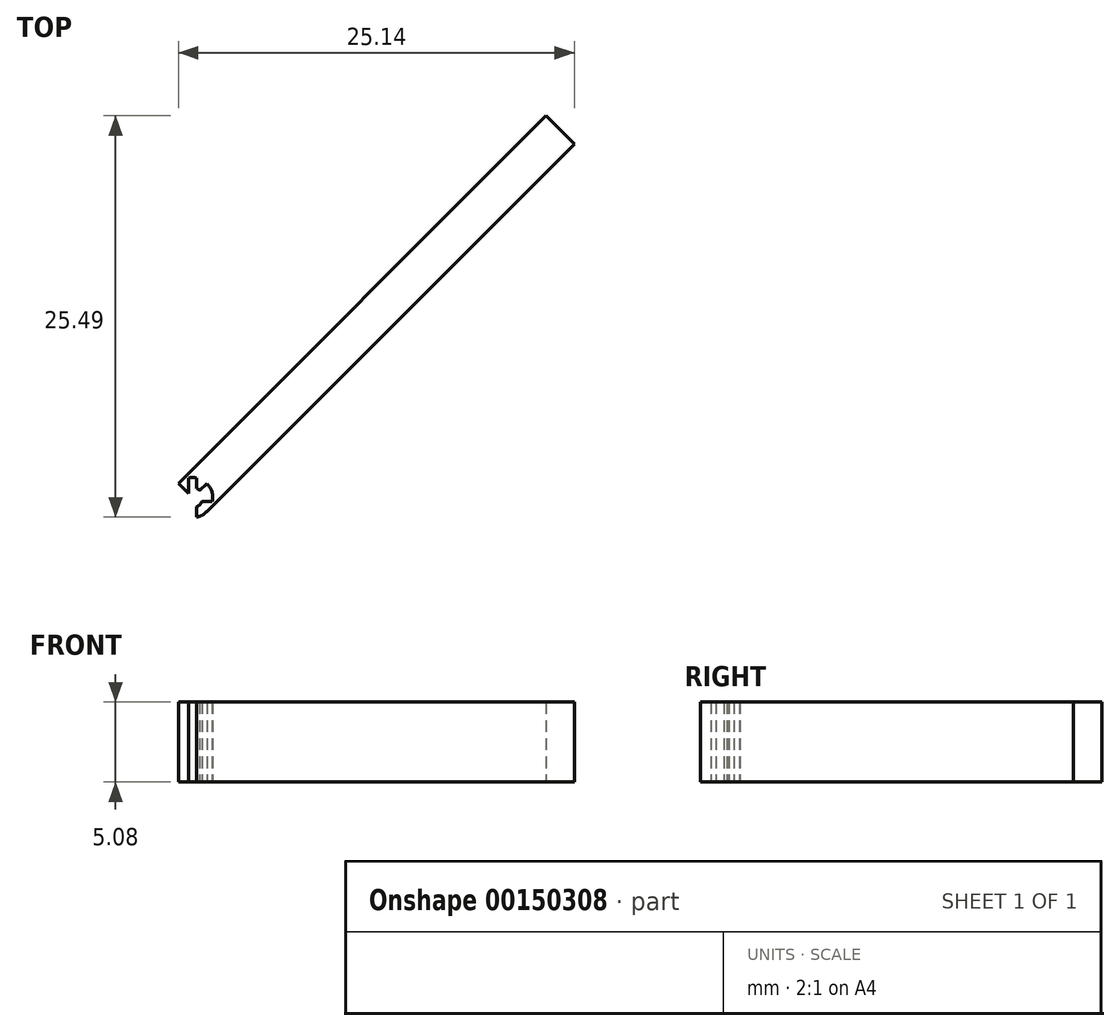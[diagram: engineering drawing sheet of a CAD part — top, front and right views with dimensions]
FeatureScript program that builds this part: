
annotation { "Feature Type Name" : "Feature", "Feature Type Description" : "" }
export const myFeature = defineFeature(function(context is Context, id is Id, definition is map)
    precondition{}
    {
        {
            var Q0;
            Q0=qCreatedBy(makeId("Top.planeOp"),FACE);
            var sketch = newSketch(context, id + "F0", { "sketchPlane" : qUnion([Q0])});
            skCircle(sketch, "E0", {"center": v(0, 0) * mm, "radius": 0.64 * mm});
            skCircle(sketch, "E1", {"center": v(0, 0) * mm, "radius": 1.27 * mm});
            skLineSegment(sketch, "E2.bottom", {"start": v(2.23, -1.87) * mm, "end": v(-1.87, 2.23) * mm});
            skLineSegment(sketch, "E2.top", {"start": v(1.87, -2.23) * mm, "end": v(-2.23, 1.87) * mm});
            skLineSegment(sketch, "E2.left", {"start": v(2.23, -1.87) * mm, "end": v(1.87, -2.23) * mm});
            skLineSegment(sketch, "E2.right", {"start": v(-1.87, 2.23) * mm, "end": v(-2.23, 1.87) * mm});
            skLineSegment(sketch, "E3.bottom", {"start": v(1.27, 0) * mm, "end": v(-1.27, 0) * mm});
            skLineSegment(sketch, "E3.top", {"start": v(1.27, 33.02) * mm, "end": v(-1.27, 33.02) * mm});
            skLineSegment(sketch, "E3.left", {"start": v(1.27, 0) * mm, "end": v(1.27, 33.02) * mm});
            skLineSegment(sketch, "E3.right", {"start": v(-1.27, 0) * mm, "end": v(-1.27, 33.02) * mm});
            skLineSegment(sketch, "E4", {"start": v(0, 0) * mm, "end": v(0.18, 0.18) * mm});
            skLineSegment(sketch, "E5", {"start": v(0, 0) * mm, "end": v(0, 1.27) * mm});
            skLineSegment(sketch, "E6.MirrorCS", {"start": v(-2.23, -1.87) * mm, "end": v(1.87, 2.23) * mm});
            skLineSegment(sketch, "E7.MirrorCS", {"start": v(-1.87, -2.23) * mm, "end": v(2.23, 1.87) * mm});
            skSolve(sketch);
        }
        {
            var Q0;
            {var subQ0=sQuery(id+"F0.wireOp",EDGE,"BzvpPFvM-H8qJ-Yu4j-K87A-fSPP2zc7mDrv.left");var subQ1=sQuery(id+"F0.wireOp",EDGE,"E0");var subQ2=makeQuery(id+"F0.imprint","INTERSECT",VERTEX,{"disambiguationData":[OD(0.0)],"derivedFrom":[subQ1,subQ0]});Q0=makeQuery(id+"F0.imprint","IMPRINT",FACE,{"disambiguationData":[TD([[makeQuery(id+"F0.imprint","IMPRINT",EDGE,{"disambiguationData":[TD([[subQ2,-1.0]])],"derivedFrom":subQ1}),-1.0]])]});}
            var Q1;
            {var subQ0=sQuery(id+"F0.wireOp",EDGE,"BzvpPFvM-H8qJ-Yu4j-K87A-fSPP2zc7mDrv.right");var subQ1=sQuery(id+"F0.wireOp",EDGE,"E0");var subQ2=makeQuery(id+"F0.imprint","INTERSECT",VERTEX,{"disambiguationData":[OD(0.0)],"derivedFrom":[subQ1,subQ0]});Q1=makeQuery(id+"F0.imprint","IMPRINT",FACE,{"disambiguationData":[TD([[makeQuery(id+"F0.imprint","IMPRINT",EDGE,{"disambiguationData":[TD([[subQ2,-1.0]])],"derivedFrom":subQ1}),-1.0]])]});}
            var Q2;
            {var subQ0=sQuery(id+"F0.wireOp",EDGE,"BzvpPFvM-H8qJ-Yu4j-K87A-fSPP2zc7mDrv.left");var subQ1=sQuery(id+"F0.wireOp",EDGE,"E0");var subQ2=makeQuery(id+"F0.imprint","INTERSECT",VERTEX,{"disambiguationData":[OD(0.0)],"derivedFrom":[subQ1,subQ0]});Q2=makeQuery(id+"F0.imprint","IMPRINT",FACE,{"disambiguationData":[TD([[makeQuery(id+"F0.imprint","IMPRINT",EDGE,{"disambiguationData":[TD([[subQ2,1.0]])],"derivedFrom":subQ1}),-1.0]])]});}
            var Q3;
            {var subQ0=sQuery(id+"F0.wireOp",EDGE,"E2.bottom");var subQ1=sQuery(id+"F0.wireOp",EDGE,"E0");var subQ2=makeQuery(id+"F0.imprint","INTERSECT",VERTEX,{"disambiguationData":[OD(1.0)],"derivedFrom":[subQ1,subQ0]});Q3=makeQuery(id+"F0.imprint","IMPRINT",FACE,{"disambiguationData":[TD([[makeQuery(id+"F0.imprint","IMPRINT",EDGE,{"disambiguationData":[TD([[subQ2,-1.0]])],"derivedFrom":subQ1}),-1.0]])]});}
            var Q4;
            {var subQ0=sQuery(id+"F0.wireOp",EDGE,"E2.bottom");var subQ1=sQuery(id+"F0.wireOp",EDGE,"E0");var subQ2=makeQuery(id+"F0.imprint","INTERSECT",VERTEX,{"disambiguationData":[OD(0.0)],"derivedFrom":[subQ1,subQ0]});Q4=makeQuery(id+"F0.imprint","IMPRINT",FACE,{"disambiguationData":[TD([[makeQuery(id+"F0.imprint","IMPRINT",EDGE,{"disambiguationData":[TD([[subQ2,1.0]])],"derivedFrom":subQ1}),-1.0]])]});}
            var Q5;
            {var subQ0=sQuery(id+"F0.wireOp",EDGE,"BzvpPFvM-H8qJ-Yu4j-K87A-fSPP2zc7mDrv.left");var subQ1=sQuery(id+"F0.wireOp",EDGE,"E0");var subQ2=makeQuery(id+"F0.imprint","INTERSECT",VERTEX,{"disambiguationData":[OD(1.0)],"derivedFrom":[subQ1,subQ0]});Q5=makeQuery(id+"F0.imprint","IMPRINT",FACE,{"disambiguationData":[TD([[makeQuery(id+"F0.imprint","IMPRINT",EDGE,{"disambiguationData":[TD([[subQ2,-1.0]])],"derivedFrom":subQ1}),-1.0]])]});}
            var Q6;
            {var subQ0=sQuery(id+"F0.wireOp",EDGE,"E2.top");var subQ1=sQuery(id+"F0.wireOp",EDGE,"E0");var subQ2=makeQuery(id+"F0.imprint","INTERSECT",VERTEX,{"disambiguationData":[OD(0.0)],"derivedFrom":[subQ1,subQ0]});Q6=makeQuery(id+"F0.imprint","IMPRINT",FACE,{"disambiguationData":[TD([[makeQuery(id+"F0.imprint","IMPRINT",EDGE,{"disambiguationData":[TD([[subQ2,-1.0]])],"derivedFrom":subQ1}),-1.0]])]});}
            var Q7;
            {var subQ0=sQuery(id+"F0.wireOp",EDGE,"BzvpPFvM-H8qJ-Yu4j-K87A-fSPP2zc7mDrv.right");var subQ1=sQuery(id+"F0.wireOp",EDGE,"E0");var subQ2=makeQuery(id+"F0.imprint","INTERSECT",VERTEX,{"disambiguationData":[OD(1.0)],"derivedFrom":[subQ1,subQ0]});Q7=makeQuery(id+"F0.imprint","IMPRINT",FACE,{"disambiguationData":[TD([[makeQuery(id+"F0.imprint","IMPRINT",EDGE,{"disambiguationData":[TD([[subQ2,-1.0]])],"derivedFrom":subQ1}),-1.0]])]});}
            var Q8;
            {var subQ0=sQuery(id+"F0.wireOp",EDGE,"BzvpPFvM-H8qJ-Yu4j-K87A-fSPP2zc7mDrv.right");var subQ1=sQuery(id+"F0.wireOp",EDGE,"E0");var subQ2=makeQuery(id+"F0.imprint","INTERSECT",VERTEX,{"disambiguationData":[OD(0.0)],"derivedFrom":[subQ1,subQ0]});Q8=makeQuery(id+"F0.imprint","IMPRINT",FACE,{"disambiguationData":[TD([[makeQuery(id+"F0.imprint","IMPRINT",EDGE,{"disambiguationData":[TD([[subQ2,-1.0]])],"derivedFrom":subQ1}),1.0]])]});}
            var Q9;
            {var subQ0=sQuery(id+"F0.wireOp",EDGE,"BzvpPFvM-H8qJ-Yu4j-K87A-fSPP2zc7mDrv.left");var subQ1=sQuery(id+"F0.wireOp",EDGE,"E0");var subQ2=makeQuery(id+"F0.imprint","INTERSECT",VERTEX,{"disambiguationData":[OD(0.0)],"derivedFrom":[subQ1,subQ0]});Q9=makeQuery(id+"F0.imprint","IMPRINT",FACE,{"disambiguationData":[TD([[makeQuery(id+"F0.imprint","IMPRINT",EDGE,{"disambiguationData":[TD([[subQ2,1.0]])],"derivedFrom":subQ1}),1.0]])]});}
            var Q10;
            {var subQ0=sQuery(id+"F0.wireOp",EDGE,"E2.top");var subQ1=sQuery(id+"F0.wireOp",EDGE,"E0");var subQ2=makeQuery(id+"F0.imprint","INTERSECT",VERTEX,{"disambiguationData":[OD(0.0)],"derivedFrom":[subQ1,subQ0]});Q10=makeQuery(id+"F0.imprint","IMPRINT",FACE,{"disambiguationData":[TD([[makeQuery(id+"F0.imprint","IMPRINT",EDGE,{"disambiguationData":[TD([[subQ2,-1.0]])],"derivedFrom":subQ1}),1.0]])]});}
            var Q11;
            {var subQ0=sQuery(id+"F0.wireOp",EDGE,"BzvpPFvM-H8qJ-Yu4j-K87A-fSPP2zc7mDrv.left");var subQ1=sQuery(id+"F0.wireOp",EDGE,"E0");var subQ2=makeQuery(id+"F0.imprint","INTERSECT",VERTEX,{"disambiguationData":[OD(1.0)],"derivedFrom":[subQ1,subQ0]});Q11=makeQuery(id+"F0.imprint","IMPRINT",FACE,{"disambiguationData":[TD([[makeQuery(id+"F0.imprint","IMPRINT",EDGE,{"disambiguationData":[TD([[subQ2,-1.0]])],"derivedFrom":subQ1}),1.0]])]});}
            var Q12;
            {var subQ0=sQuery(id+"F0.wireOp",EDGE,"E3.bottom");var subQ1=sQuery(id+"F0.wireOp",EDGE,"E0");var subQ2=makeQuery(id+"F0.imprint","INTERSECT",VERTEX,{"disambiguationData":[OD(1.0)],"derivedFrom":[subQ1,subQ0]});Q12=makeQuery(id+"F0.imprint","IMPRINT",FACE,{"disambiguationData":[TD([[makeQuery(id+"F0.imprint","IMPRINT",EDGE,{"disambiguationData":[TD([[subQ2,-1.0]])],"derivedFrom":subQ1}),-1.0]])]});}
            var Q13;
            {var subQ0=sQuery(id+"F0.wireOp",EDGE,"E3.bottom");var subQ1=sQuery(id+"F0.wireOp",EDGE,"E0");var subQ2=makeQuery(id+"F0.imprint","INTERSECT",VERTEX,{"disambiguationData":[OD(0.0)],"derivedFrom":[subQ1,subQ0]});Q13=makeQuery(id+"F0.imprint","IMPRINT",FACE,{"disambiguationData":[TD([[makeQuery(id+"F0.imprint","IMPRINT",EDGE,{"disambiguationData":[TD([[subQ2,1.0]])],"derivedFrom":subQ1}),-1.0]])]});}
            var Q14;
            {var subQ5=sQuery(id+"F0.wireOp",EDGE,"BzvpPFvM-H8qJ-Yu4j-K87A-fSPP2zc7mDrv.bottom");Q14=makeQuery(id+"F0.imprint","IMPRINT",FACE,{"disambiguationData":[TD([[makeQuery(id+"F0.imprint","IMPRINT",EDGE,{"derivedFrom":subQ5}),1.0]])]});}
            var Q15;
            {var subQ10=sQuery(id+"F0.wireOp",EDGE,"BzvpPFvM-H8qJ-Yu4j-K87A-fSPP2zc7mDrv.bottom");Q15=makeQuery(id+"F0.imprint","IMPRINT",FACE,{"disambiguationData":[TD([[makeQuery(id+"F0.imprint","IMPRINT",EDGE,{"derivedFrom":subQ10}),-1.0]])]});}
            var Q16;
            {var subQ0=sQuery(id+"F0.wireOp",EDGE,"E3.right");var subQ3=sQuery(id+"F0.wireOp",EDGE,"E2.bottom");var subQ5=makeQuery(id+"F0.imprint","INTERSECT",VERTEX,{"derivedFrom":[subQ3,subQ0]});Q16=makeQuery(id+"F0.imprint","IMPRINT",FACE,{"disambiguationData":[TD([[makeQuery(id+"F0.imprint","IMPRINT",EDGE,{"disambiguationData":[TD([[subQ5,1.0]])],"derivedFrom":subQ3}),1.0]])]});}
            var Q17;
            {var subQ0=sQuery(id+"F0.wireOp",EDGE,"E3.left");var subQ3=sQuery(id+"F0.wireOp",EDGE,"E7.MirrorCS");var subQ5=makeQuery(id+"F0.imprint","INTERSECT",VERTEX,{"derivedFrom":[subQ0,subQ3]});Q17=makeQuery(id+"F0.imprint","IMPRINT",FACE,{"disambiguationData":[TD([[makeQuery(id+"F0.imprint","IMPRINT",EDGE,{"disambiguationData":[TD([[subQ5,1.0]])],"derivedFrom":subQ3}),-1.0]])]});}
            var Q18;
            {var subQ0=sQuery(id+"F0.wireOp",EDGE,"E7.MirrorCS");var subQ1=sQuery(id+"F0.wireOp",EDGE,"E1");var subQ2=makeQuery(id+"F0.imprint","INTERSECT",VERTEX,{"disambiguationData":[OD(1.0)],"derivedFrom":[subQ1,subQ0]});Q18=makeQuery(id+"F0.imprint","IMPRINT",FACE,{"disambiguationData":[TD([[makeQuery(id+"F0.imprint","IMPRINT",EDGE,{"disambiguationData":[TD([[subQ2,-1.0]])],"derivedFrom":subQ1}),-1.0]])]});}
            var Q19;
            {var subQ0=sQuery(id+"F0.wireOp",EDGE,"E3.top");Q19=makeQuery(id+"F0.imprint","IMPRINT",FACE,{"disambiguationData":[TD([[makeQuery(id+"F0.imprint","IMPRINT",EDGE,{"derivedFrom":subQ0}),1.0]])]});}
            var Q20;
            {var subQ0=sQuery(id+"F0.wireOp",EDGE,"E3.right");var subQ3=sQuery(id+"F0.wireOp",EDGE,"E2.top");var subQ5=makeQuery(id+"F0.imprint","INTERSECT",VERTEX,{"derivedFrom":[subQ3,subQ0]});Q20=makeQuery(id+"F0.imprint","IMPRINT",FACE,{"disambiguationData":[TD([[makeQuery(id+"F0.imprint","IMPRINT",EDGE,{"disambiguationData":[TD([[subQ5,1.0]])],"derivedFrom":subQ3}),1.0]])]});}
            extrude(context, id + "F1", {"entities" : qUnion([Q0, Q1, Q2, Q3, Q4, Q5, Q6, Q7, Q8, Q9, Q10, Q11, Q12, Q13, Q14, Q15, Q16, Q17, Q18, Q19, Q20]), "depth" : 5.08 * mm});
        }
        {
            var Q0;
            Q0=makeQuery(id+"F1.opExtrude","SWEPT_BODY",BODY,{"disambiguationData":[OSD([sQuery(id+"F0.wireOp",EDGE,"E0"),sQuery(id+"F0.wireOp",EDGE,"E1"),sQuery(id+"F0.wireOp",EDGE,"E2.bottom"),sQuery(id+"F0.wireOp",EDGE,"E2.top"),sQuery(id+"F0.wireOp",EDGE,"E3.top"),sQuery(id+"F0.wireOp",EDGE,"E3.left"),sQuery(id+"F0.wireOp",EDGE,"E3.right"),sQuery(id+"F0.wireOp",EDGE,"E6.MirrorCS"),sQuery(id+"F0.wireOp",EDGE,"E7.MirrorCS")])]});
            var Q1;
            Q1=makeQuery(id+"F1.opExtrude","SWEPT_EDGE",EDGE,{"disambiguationData":[OSD([sQuery(id+"F0.wireOp",EDGE,"E1"),sQuery(id+"F0.wireOp",EDGE,"E3.bottom"),sQuery(id+"F0.wireOp",EDGE,"E3.right")])]});
            transform(context, id + "F2", {"entities" : qUnion([Q0]), "transformType" : TransformType.ROTATION, "transformAxis" : qUnion([Q1]), "angle" : 45 * degree, "makeCopy" : false});
        }
    });
